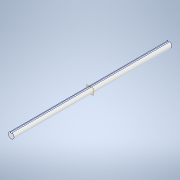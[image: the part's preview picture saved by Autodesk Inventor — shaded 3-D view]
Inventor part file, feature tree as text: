
AUTODESK INVENTOR PART (.ipt)
format: ipt  version: 2021 (Build 250183000, 183)  size: 101,888 bytes
history: native  units: in
note: dims shown in document units (in); Inventor stores cm internally (conversion verified against a paired STEP export)
features: extrude x1, sketch x1
ambient origin geometry x8: Origin, YZ Plane, XZ Plane, XY Plane, X Axis, Y Axis, Z Axis, Center Point
bodies: Solid1 (feature_tree)
feature tree (2):
  extrude  "Extrusion1"  Depth=10.0in
  sketch  "Sketch1"  dims[d0=0.375in d1=0.0469in d2=0.0628in d3=10.0in d4=0.0in]
